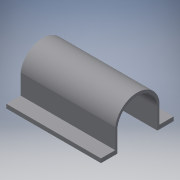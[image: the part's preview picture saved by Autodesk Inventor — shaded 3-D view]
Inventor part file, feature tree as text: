
AUTODESK INVENTOR PART (.ipt)
format: ipt  version: 2016 SP1 (Build 200210100, 210)  size: 115,200 bytes
history: native  units: in
note: dims shown in document units (in); Inventor stores cm internally (conversion verified against a paired STEP export)
features: extrude x1, sketch x1
ambient origin geometry x8: Origin, YZ Plane, XZ Plane, XY Plane, X Axis, Y Axis, Z Axis, Center Point
bodies: Solid1 (feature_tree)
feature tree (2):
  extrude  "Extrusion1"  Depth=0.5488in
  sketch  "Sketch1"  dims[d0=0.9843in d9=0.5421in d11=0.4921in d12=2.3228in d13=0.0in d40=0.4921in d41=0.4in d42=0.1in d44=0.4921in d45=0.4in d46=0.1in d47=0.05in d48=0.05in d50=0.5488in d51=0.4068in d52=0.0147in d20=1.0in d21=1.0in]
